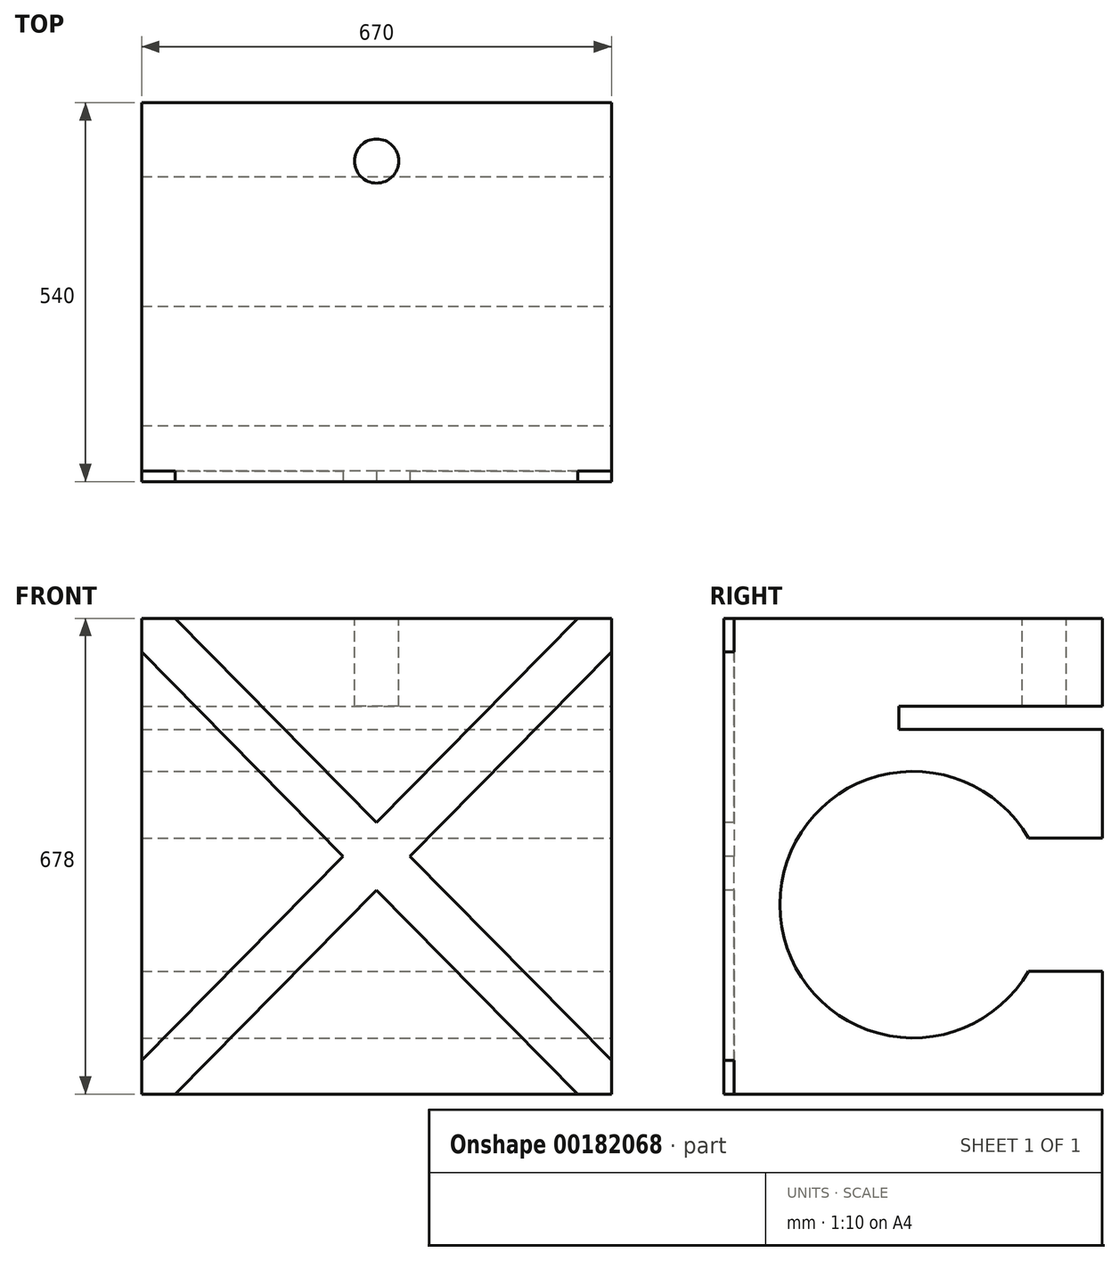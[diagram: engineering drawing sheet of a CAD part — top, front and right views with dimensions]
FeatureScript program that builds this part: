
annotation { "Feature Type Name" : "Feature", "Feature Type Description" : "" }
export const myFeature = defineFeature(function(context is Context, id is Id, definition is map)
    precondition{}
    {
        {
            var Q0;
            Q0=qCreatedBy(makeId("Front.planeOp"),FACE);
            var sketch = newSketch(context, id + "F0", { "sketchPlane" : qUnion([Q0])});
            skLineSegment(sketch, "E0.bottom", {"start": v(-333.06, 403.87) * mm, "end": v(336.94, 403.87) * mm});
            skLineSegment(sketch, "E0.top", {"start": v(-333.06, -274.13) * mm, "end": v(336.94, -274.13) * mm});
            skLineSegment(sketch, "E0.left", {"start": v(-333.06, 403.87) * mm, "end": v(-333.06, -274.13) * mm});
            skLineSegment(sketch, "E0.right", {"start": v(336.94, 403.87) * mm, "end": v(336.94, -274.13) * mm});
            skSolve(sketch);
        }
        {
            var Q0;
            Q0 = qSketchRegion(id + "F0", true);
            extrude(context, id + "F1", {"entities" : qUnion([Q0]), "oppositeDirection" : true, "depth" : 540 * mm});
        }
        {
            var Q0;
            Q0=makeQuery(id+"F1.opExtrude","SWEPT_FACE",FACE,{"disambiguationData":[OSD([sQuery(id+"F0.wireOp",EDGE,"E0.bottom")])]});
            var sketch = newSketch(context, id + "F2", { "sketchPlane" : qUnion([Q0])});
            skCircle(sketch, "E1", {"center": v(1.94, 457) * mm, "radius": 31.5 * mm});
            skSolve(sketch);
        }
        {
            var Q0;
            Q0 = qSketchRegion(id + "F2", true);
            extrude(context, id + "F3", {"entities" : qUnion([Q0]), "operationType" : NewBodyOperationType.REMOVE, "oppositeDirection" : true, "depth" : 125 * mm});
        }
        {
            var Q0;
            Q0=makeQuery(id+"F1.opExtrude","SWEPT_FACE",FACE,{"disambiguationData":[OSD([sQuery(id+"F0.wireOp",EDGE,"E0.right")])]});
            var sketch = newSketch(context, id + "F4", { "sketchPlane" : qUnion([Q0])});
            skLineSegment(sketch, "E2", {"start": v(540, 278.87) * mm, "end": v(540, 245.87) * mm});
            skLineSegment(sketch, "E3", {"start": v(540, 278.87) * mm, "end": v(250, 278.87) * mm});
            skLineSegment(sketch, "E4", {"start": v(540, 245.87) * mm, "end": v(250, 245.87) * mm});
            skLineSegment(sketch, "E5", {"start": v(250, 278.87) * mm, "end": v(250, 245.87) * mm});
            skSolve(sketch);
        }
        {
            var Q0;
            Q0 = qSketchRegion(id + "F4", true);
            extrude(context, id + "F5", {"entities" : qUnion([Q0]), "operationType" : NewBodyOperationType.REMOVE, "oppositeDirection" : true, "depth" : 670 * mm});
        }
        {
            var Q0;
            Q0=makeQuery(id+"F1.opExtrude","SWEPT_FACE",FACE,{"disambiguationData":[OSD([sQuery(id+"F0.wireOp",EDGE,"E0.right")])]});
            var sketch = newSketch(context, id + "F6", { "sketchPlane" : qUnion([Q0])});
            skCircle(sketch, "E6", {"center": v(270, -4.13) * mm, "radius": 190 * mm});
            skSolve(sketch);
        }
        {
            var Q0;
            Q0 = qSketchRegion(id + "F6", true);
            extrude(context, id + "F7", {"entities" : qUnion([Q0]), "operationType" : NewBodyOperationType.REMOVE, "oppositeDirection" : true, "depth" : 670 * mm});
        }
        {
            var Q0;
            Q0=makeQuery(id+"F1.opExtrude","SWEPT_FACE",FACE,{"disambiguationData":[OSD([sQuery(id+"F0.wireOp",EDGE,"E0.right")])]});
            var sketch = newSketch(context, id + "F8", { "sketchPlane" : qUnion([Q0])});
            skLineSegment(sketch, "E7", {"start": v(540, -99.13) * mm, "end": v(540, 90.87) * mm});
            skLineSegment(sketch, "E8", {"start": v(540, 90.87) * mm, "end": v(434.54, 90.87) * mm});
            skLineSegment(sketch, "E9", {"start": v(540, -99.13) * mm, "end": v(434.54, -99.13) * mm});
            skPoint(sketch, "E10.endSnap0", {"position": v(487.27, 90.87) * mm});
            skLineSegment(sketch, "E11", {"start": v(434.54, 90.87) * mm, "end": v(434.54, -99.13) * mm});
            skSolve(sketch);
        }
        {
            var Q0;
            Q0 = qSketchRegion(id + "F8", true);
            extrude(context, id + "F9", {"entities" : qUnion([Q0]), "operationType" : NewBodyOperationType.REMOVE, "oppositeDirection" : true, "depth" : 670 * mm});
        }
        {
            var Q0;
            Q0=makeQuery(id+"F1.opExtrude","CAP_FACE",FACE,{"disambiguationData":[OSD([sQuery(id+"F0.wireOp",EDGE,"E0.bottom"),sQuery(id+"F0.wireOp",EDGE,"E0.top"),sQuery(id+"F0.wireOp",EDGE,"E0.left"),sQuery(id+"F0.wireOp",EDGE,"E0.right")])],"isStart":true});
            var sketch = newSketch(context, id + "F10", { "sketchPlane" : qUnion([Q0])});
            skLineSegment(sketch, "E12", {"start": v(-333.06, 403.87) * mm, "end": v(-285.06, 403.87) * mm});
            skLineSegment(sketch, "E13", {"start": v(-333.06, 403.87) * mm, "end": v(-333.06, 355.87) * mm});
            skLineSegment(sketch, "E14", {"start": v(336.94, -274.13) * mm, "end": v(336.94, -226.13) * mm});
            skLineSegment(sketch, "E15", {"start": v(336.94, -274.13) * mm, "end": v(288.94, -274.13) * mm});
            skLineSegment(sketch, "E16", {"start": v(-333.06, -274.13) * mm, "end": v(-333.06, -226.13) * mm});
            skLineSegment(sketch, "E17", {"start": v(-333.06, -274.13) * mm, "end": v(-285.06, -274.13) * mm});
            skLineSegment(sketch, "E18", {"start": v(336.94, 403.87) * mm, "end": v(288.94, 403.87) * mm});
            skLineSegment(sketch, "E19", {"start": v(336.94, 403.87) * mm, "end": v(336.94, 355.87) * mm});
            skLineSegment(sketch, "E20", {"start": v(-333.06, -226.13) * mm, "end": v(-45.75, 64.87) * mm});
            skLineSegment(sketch, "E21", {"start": v(-45.75, 64.87) * mm, "end": v(-333.06, 355.87) * mm});
            skLineSegment(sketch, "E22", {"start": v(-285.06, 403.87) * mm, "end": v(1.94, 113.17) * mm});
            skLineSegment(sketch, "E23", {"start": v(1.94, 113.17) * mm, "end": v(288.94, 403.87) * mm});
            skLineSegment(sketch, "E24", {"start": v(336.94, 355.87) * mm, "end": v(49.64, 64.87) * mm});
            skLineSegment(sketch, "E25", {"start": v(49.64, 64.87) * mm, "end": v(336.94, -226.13) * mm});
            skLineSegment(sketch, "E26", {"start": v(288.94, -274.13) * mm, "end": v(1.94, 16.56) * mm});
            skLineSegment(sketch, "E27", {"start": v(1.94, 16.56) * mm, "end": v(-285.06, -274.13) * mm});
            skSolve(sketch);
        }
        {
            var Q0;
            Q0 = qSketchRegion(id + "F10", true);
            extrude(context, id + "F11", {"entities" : qUnion([Q0]), "operationType" : NewBodyOperationType.REMOVE, "oppositeDirection" : true, "depth" : 15 * mm});
        }
    });
